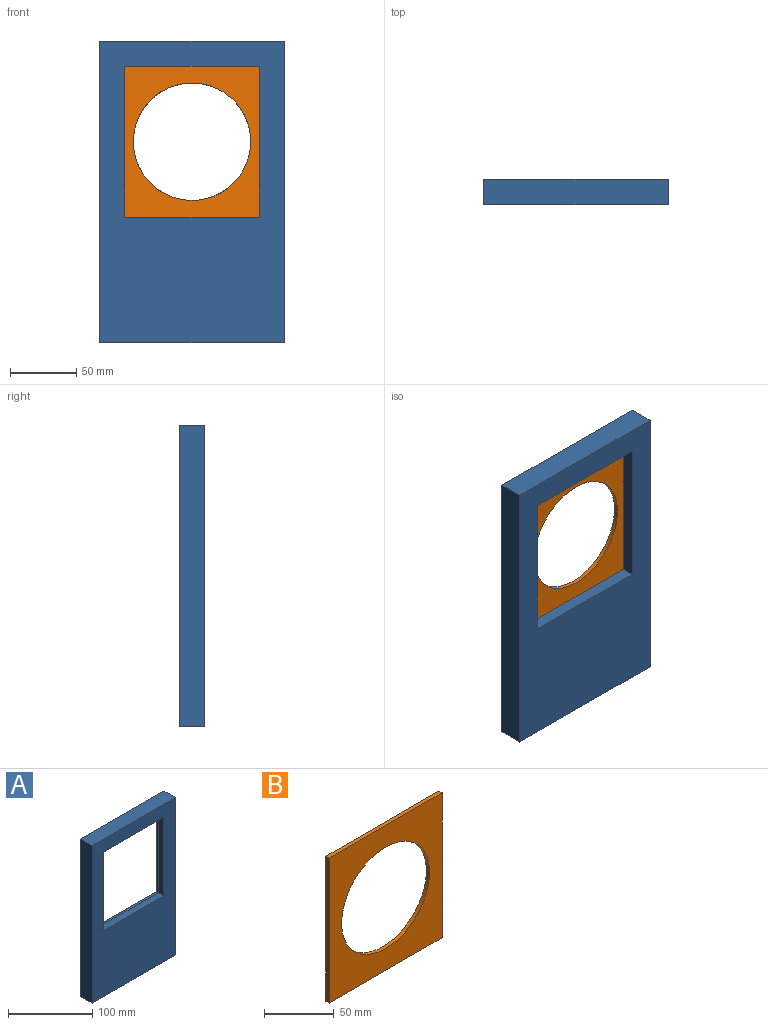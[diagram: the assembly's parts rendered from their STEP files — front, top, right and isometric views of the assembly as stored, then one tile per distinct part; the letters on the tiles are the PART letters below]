
ASSEMBLY  parts=2 mates=1
PART A: 15 faces, bbox 139.7x19.1x228.6 mm
  f0: plane 228.6x139.7mm, normal (0,1,0), area 17419.3mm2, adj f6,f7,f8,f9,f10,f11,f12,f13
  f1: plane 101.6x9.53mm, normal (0,0,1), area 967.7mm2, adj f2,f4,f5,f14
  f2: plane 114.3x9.53mm, normal (1,0,0), area 1088.7mm2, adj f1,f3,f5,f14
  f3: plane 101.6x9.53mm, normal (0,0,-1), area 967.7mm2, adj f2,f4,f5,f14
  f4: plane 114.3x9.53mm, normal (-1,0,0), area 1088.7mm2, adj f1,f3,f5,f14
  f5: plane 228.6x139.7mm, normal (0,-1,0), area 20322.5mm2, adj f1,f2,f3,f4,f6,f7,f8,f9
  f6: plane 139.7x19.05mm, normal (0,0,1), area 2661.3mm2, adj f0,f5,f7,f9
  f7: plane 228.6x19.05mm, normal (-1,0,0), area 4354.8mm2, adj f0,f5,f6,f8
  f8: plane 139.7x19.05mm, normal (0,0,-1), area 2661.3mm2, adj f0,f5,f7,f9
  f9: plane 228.6x19.05mm, normal (1,0,0), area 4354.8mm2, adj f0,f5,f6,f8
  f10: plane 114.3x9.53mm, normal (0,0,1), area 1088.7mm2, adj f0,f11,f13,f14
  f11: plane 127x9.53mm, normal (1,0,0), area 1209.7mm2, adj f0,f10,f12,f14
  f12: plane 114.3x9.53mm, normal (0,0,-1), area 1088.7mm2, adj f0,f11,f13,f14
  f13: plane 127x9.53mm, normal (-1,0,0), area 1209.7mm2, adj f0,f10,f12,f14
  f14: plane 127x114.3mm, normal (0,1,0), area 2903.2mm2, adj f1,f2,f3,f4,f10,f11,f12,f13
PART B: 7 faces, bbox 114.3x3.2x127 mm
  f0: plane 114.3x3.18mm, normal (0,0,1), area 362.9mm2, adj f1,f3,f4,f5
  f1: plane 127x3.18mm, normal (-1,0,0), area 403.2mm2, adj f0,f2,f4,f5
  f2: plane 114.3x3.18mm, normal (0,0,-1), area 362.9mm2, adj f1,f3,f4,f5
  f3: plane 127x3.18mm, normal (1,0,0), area 403.2mm2, adj f0,f2,f4,f5
  f4: plane 127x114.3mm, normal (0,1,0), area 8308.9mm2, adj f0,f1,f2,f3,f6
  f5: plane 127x114.3mm, normal (0,-1,0), area 8308.9mm2, adj f0,f1,f2,f3,f6
  f6: cylinder r=44.45mm len=88.9mm, axis (0,-1,0), area 886.7mm2, adj f4,f5
PLACE A at identity
PLACE B t=(-203.2,9.52,88.9)mm
MATE fastened B.f5 <-> A.f14  axis (0,-1,0) through (12.7,9.52,215.9)mm
